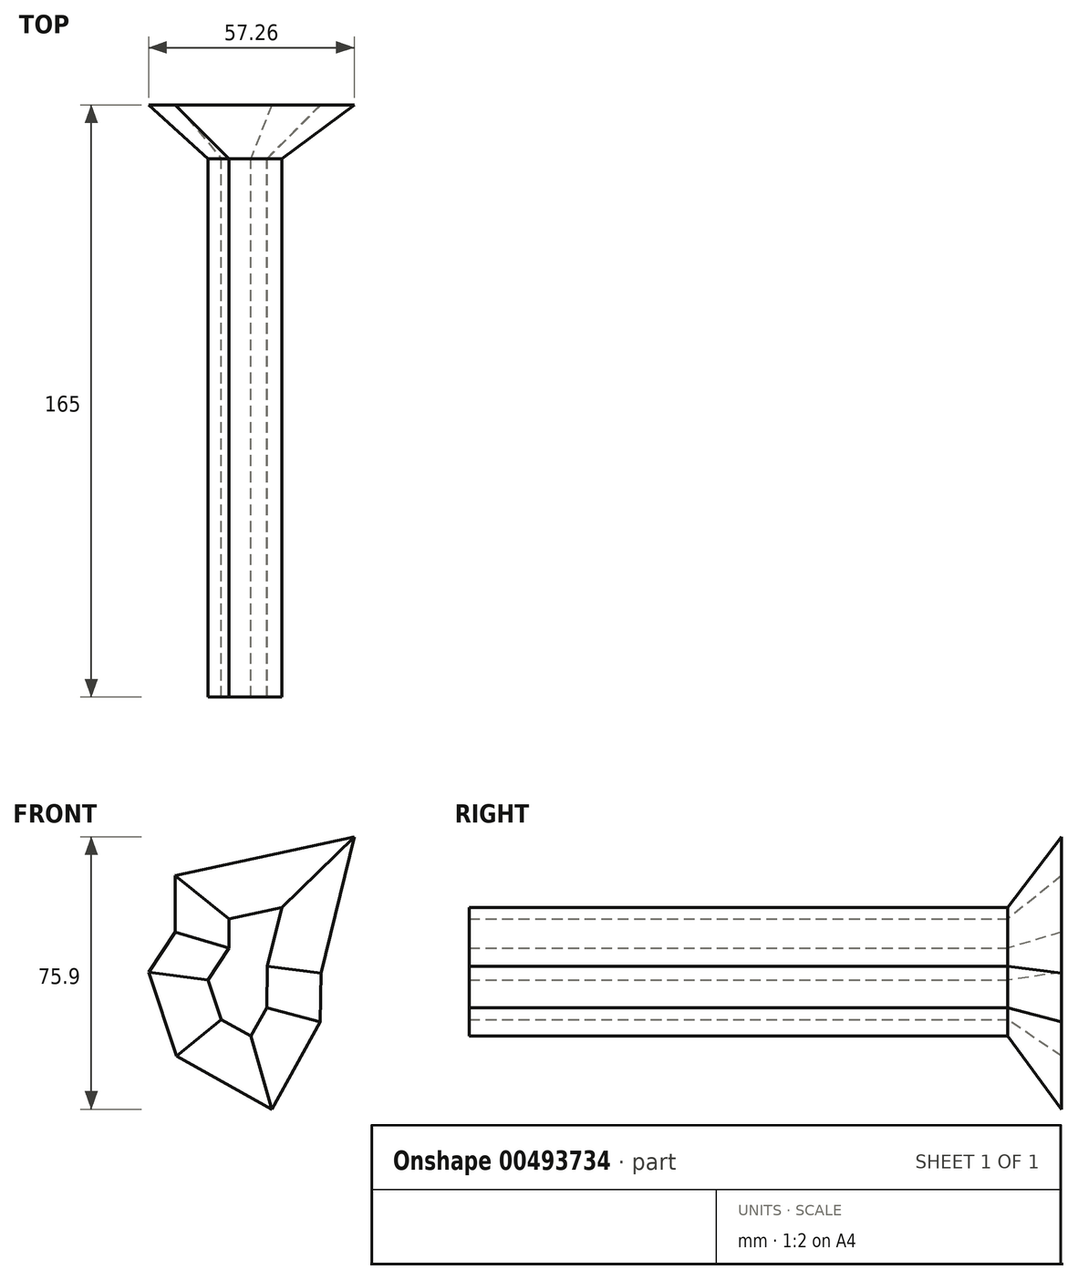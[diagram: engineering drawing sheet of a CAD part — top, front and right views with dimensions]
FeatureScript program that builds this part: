
annotation { "Feature Type Name" : "Feature", "Feature Type Description" : "" }
export const myFeature = defineFeature(function(context is Context, id is Id, definition is map)
    precondition{}
    {
        {
            var Q0;
            Q0=qCreatedBy(makeId("Front.planeOp"),FACE);
            var sketch = newSketch(context, id + "F0", { "sketchPlane" : qUnion([Q0])});
            skLineSegment(sketch, "E0", {"start": v(-4.2, 6.94) * mm, "end": v(-10.08, -1.96) * mm});
            skLineSegment(sketch, "E1", {"start": v(-10.08, -1.96) * mm, "end": v(-6.43, -12.93) * mm});
            skLineSegment(sketch, "E2", {"start": v(-6.43, -12.93) * mm, "end": v(1.83, -17.53) * mm});
            skLineSegment(sketch, "E3", {"start": v(1.83, -17.53) * mm, "end": v(6.24, -9.62) * mm});
            skLineSegment(sketch, "E4", {"start": v(6.24, -9.62) * mm, "end": v(6.44, 1.85) * mm});
            skLineSegment(sketch, "E5", {"start": v(6.44, 1.85) * mm, "end": v(10.41, 18.22) * mm});
            skLineSegment(sketch, "E6", {"start": v(10.41, 18.22) * mm, "end": v(-4.2, 15.04) * mm});
            skLineSegment(sketch, "E7", {"start": v(-4.2, 15.04) * mm, "end": v(-4.2, 6.94) * mm});
            skSolve(sketch);
        }
        {
            var Q0;
            Q0=makeQuery(id+"F0.imprint","IMPRINT",FACE,{"disambiguationData":[TD([[makeQuery(id+"F0.imprint","IMPRINT",EDGE,{"derivedFrom":sQuery(id+"F0.wireOp",EDGE,"E0")}),1.0]])]});
            var Q1;
            Q1=sQuery(id+"F0.wireOp",EDGE,"E0");
            var Q2;
            Q2=sQuery(id+"F0.wireOp",EDGE,"E1");
            var Q3;
            Q3=sQuery(id+"F0.wireOp",EDGE,"E2");
            var Q4;
            Q4=sQuery(id+"F0.wireOp",EDGE,"E3");
            var Q5;
            Q5=sQuery(id+"F0.wireOp",EDGE,"E4");
            var Q6;
            Q6=sQuery(id+"F0.wireOp",EDGE,"E5");
            var Q7;
            Q7=sQuery(id+"F0.wireOp",EDGE,"E6");
            var Q8;
            Q8=sQuery(id+"F0.wireOp",EDGE,"E7");
            extrude(context, id + "F1", {"entities" : qUnion([Q0]), "surfaceEntities" : qUnion([Q1, Q2, Q3, Q4, Q5, Q6, Q7, Q8]), "depth" : 150 * mm, "offsetDistance" : 25 * mm});
        }
        {
            var Q0;
            Q0=makeQuery(id+"F1.opExtrude","CAP_FACE",FACE,{"disambiguationData":[OSD([sQuery(id+"F0.wireOp",EDGE,"E0"),sQuery(id+"F0.wireOp",EDGE,"E1"),sQuery(id+"F0.wireOp",EDGE,"E2"),sQuery(id+"F0.wireOp",EDGE,"E3"),sQuery(id+"F0.wireOp",EDGE,"E4"),sQuery(id+"F0.wireOp",EDGE,"E5"),sQuery(id+"F0.wireOp",EDGE,"E6"),sQuery(id+"F0.wireOp",EDGE,"E7")])],"isStart":true});
            extrude(context, id + "F2", {"entities" : qUnion([Q0]), "operationType" : NewBodyOperationType.ADD, "depth" : 15 * mm, "offsetDistance" : 25 * mm, "hasDraft" : true, "draftAngle" : 45 * degree});
        }
    });
